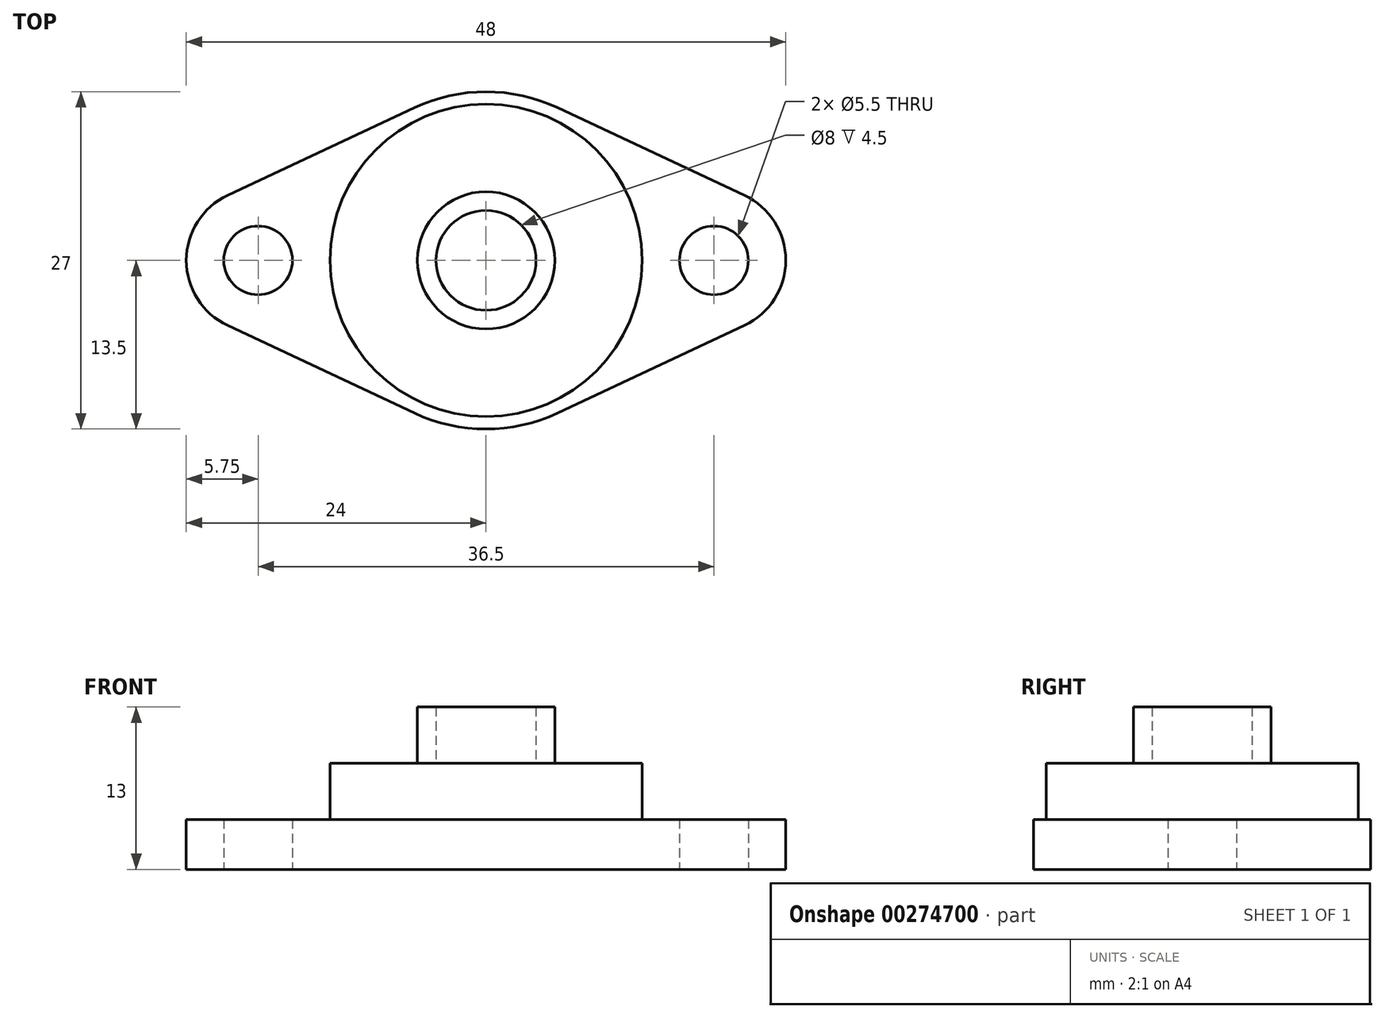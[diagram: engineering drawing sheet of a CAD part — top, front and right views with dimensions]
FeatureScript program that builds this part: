
annotation { "Feature Type Name" : "Feature", "Feature Type Description" : "" }
export const myFeature = defineFeature(function(context is Context, id is Id, definition is map)
    precondition{}
    {
        {
            var Q0;
            Q0=qCreatedBy(makeId("Top.planeOp"),FACE);
            var sketch = newSketch(context, id + "F0", { "sketchPlane" : qUnion([Q0])});
            skArc(sketch, "E0", {"start": v(-5.73, -12.22) * mm, "mid": v(0, -13.5) * mm, "end": v(5.73, -12.22) * mm});
            skCircle(sketch, "E1", {"center": v(-18.25, 0) * mm, "radius": 2.75 * mm});
            skCircle(sketch, "E2.MirrorC", {"center": v(18.25, 0) * mm, "radius": 2.75 * mm});
            skArc(sketch, "E3", {"start": v(-20.7, 5.2) * mm, "mid": v(-24, 0) * mm, "end": v(-20.7, -5.2) * mm});
            skArc(sketch, "E4.MirrorC", {"start": v(20.7, 5.2) * mm, "mid": v(24, 0) * mm, "end": v(20.7, -5.2) * mm});
            skLineSegment(sketch, "E5", {"start": v(-20.7, 5.2) * mm, "end": v(-5.73, 12.22) * mm});
            skLineSegment(sketch, "E6.MirrorCS", {"start": v(20.7, 5.2) * mm, "end": v(5.73, 12.22) * mm});
            skLineSegment(sketch, "E7.MirrorCS", {"start": v(-20.7, -5.2) * mm, "end": v(-5.73, -12.22) * mm});
            skLineSegment(sketch, "E8.MirrorCS", {"start": v(20.7, -5.2) * mm, "end": v(5.73, -12.22) * mm});
            skArc(sketch, "E9.trimOffspring", {"start": v(5.73, 12.22) * mm, "mid": v(0, 13.5) * mm, "end": v(-5.73, 12.22) * mm});
            skSolve(sketch);
        }
        {
            var Q0;
            Q0=qSketchRegion(id+"F0",true);
            extrude(context, id + "F1", {"entities" : qUnion([Q0]), "depth" : 4 * mm});
        }
        {
            var Q0;
            Q0=makeQuery(id+"F1.opExtrude","CAP_FACE",FACE,{"disambiguationData":[OSD([sQuery(id+"F0.wireOp",EDGE,"E0"),sQuery(id+"F0.wireOp",EDGE,"E1"),sQuery(id+"F0.wireOp",EDGE,"E2.MirrorC"),sQuery(id+"F0.wireOp",EDGE,"E3"),sQuery(id+"F0.wireOp",EDGE,"E4.MirrorC"),sQuery(id+"F0.wireOp",EDGE,"E5"),sQuery(id+"F0.wireOp",EDGE,"E6.MirrorCS"),sQuery(id+"F0.wireOp",EDGE,"E7.MirrorCS"),sQuery(id+"F0.wireOp",EDGE,"E8.MirrorCS"),sQuery(id+"F0.wireOp",EDGE,"E9.trimOffspring")])],"isStart":false});
            var sketch = newSketch(context, id + "F2", { "sketchPlane" : qUnion([Q0])});
            skCircle(sketch, "E10", {"center": v(0, 0) * mm, "radius": 12.5 * mm});
            skSolve(sketch);
        }
        {
            var Q0;
            Q0=qSketchRegion(id+"F2",true);
            extrude(context, id + "F3", {"entities" : qUnion([Q0]), "operationType" : NewBodyOperationType.ADD, "depth" : 4.5 * mm});
        }
        {
            var Q0;
            Q0=makeQuery(id+"F1.opExtrude","CAP_FACE",FACE,{"disambiguationData":[OSD([sQuery(id+"F0.wireOp",EDGE,"E0"),sQuery(id+"F0.wireOp",EDGE,"E1"),sQuery(id+"F0.wireOp",EDGE,"E2.MirrorC"),sQuery(id+"F0.wireOp",EDGE,"E3"),sQuery(id+"F0.wireOp",EDGE,"E4.MirrorC"),sQuery(id+"F0.wireOp",EDGE,"E5"),sQuery(id+"F0.wireOp",EDGE,"E6.MirrorCS"),sQuery(id+"F0.wireOp",EDGE,"E7.MirrorCS"),sQuery(id+"F0.wireOp",EDGE,"E8.MirrorCS"),sQuery(id+"F0.wireOp",EDGE,"E9.trimOffspring")])],"isStart":true});
            var sketch = newSketch(context, id + "F4", { "sketchPlane" : qUnion([Q0])});
            skCircle(sketch, "E11", {"center": v(0, 0) * mm, "radius": 4 * mm});
            skCircle(sketch, "E12", {"center": v(0, 0) * mm, "radius": 5.5 * mm});
            skSolve(sketch);
        }
        {
            var Q0;
            Q0=qSketchRegion(id+"F4",true);
            extrude(context, id + "F5", {"entities" : qUnion([Q0]), "operationType" : NewBodyOperationType.ADD, "oppositeDirection" : true, "depth" : 13 * mm});
        }
    });
